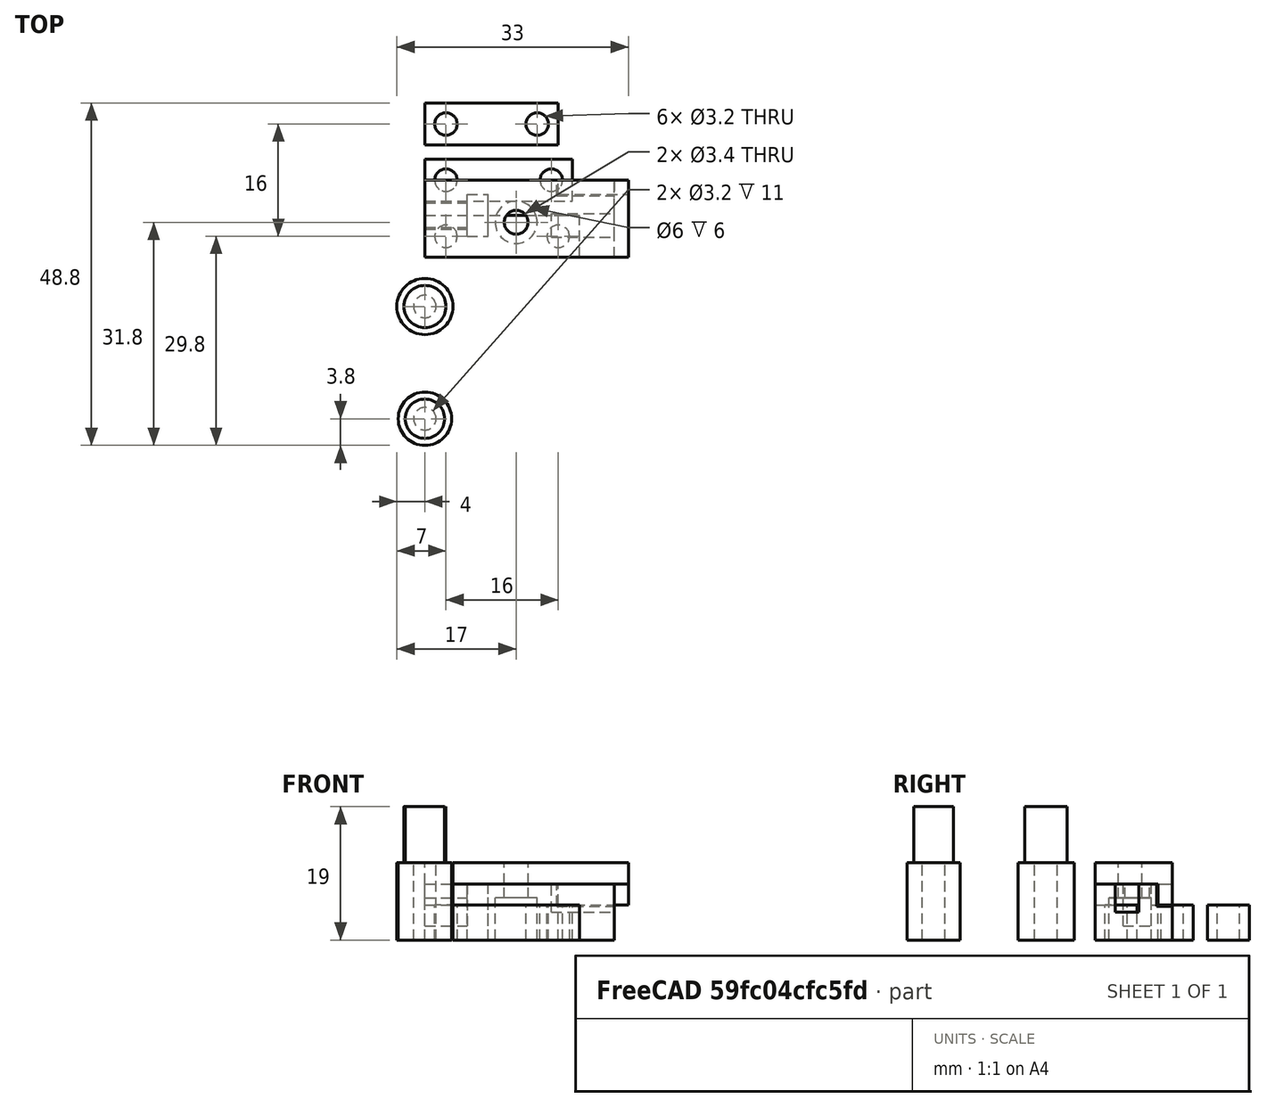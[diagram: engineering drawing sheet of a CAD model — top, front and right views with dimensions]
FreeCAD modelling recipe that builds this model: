
FCSTD DOCUMENT  (FreeCAD 0.19R24291 (Git))
Label: pb1
License: All rights reserved
LicenseURL: http://en.wikipedia.org/wiki/All_rights_reserved
objects: Part::Cylinder×15, Part::Box×11, Part::MultiFuse×7, Part::Cut×7
note: 40 computed .brp shape members not serialized (recipe doc carries the construction recipe); baked Part::Feature solids carry a one-line shape summary decoded from their .brp

FEATURE [Part::Box] Box  label="Cube"
  AttacherType = Attacher::AttachEngine3D
  Height = 8
  Length = 27
  Width = 11
FEATURE [Part::Box] Box001  label="Cube001"
  AttacherType = Attacher::AttachEngine3D
  Height = 6
  Length = 9
  Placement = pos=(0,4,2) rot=(0,0,1;0rad)
  Width = 4
FEATURE [Part::Box] Box002  label="Cube002"
  AttacherType = Attacher::AttachEngine3D
  Height = 4
  Length = 9
  Placement = pos=(18,2.85,4) rot=(0,0,1;0rad)
  Width = 3.4
FEATURE [Part::Box] Box003  label="Cube003"
  AttacherType = Attacher::AttachEngine3D
  Height = 8
  Length = 3
  Placement = pos=(6,3,0) rot=(0,0,1;0rad)
  Width = 6
FEATURE [Part::Cylinder] Cylinder
  Angle = 360
  AttacherType = Attacher::AttachEngine3D
  Height = 6
  Placement = pos=(13,5,0) rot=(0,0,1;0rad)
  Radius = 3
FEATURE [Part::Cylinder] Cylinder001
  Angle = 360
  AttacherType = Attacher::AttachEngine3D
  Height = 2
  Placement = pos=(13,5,6) rot=(0,0,1;0rad)
  Radius = 1.7
FEATURE [Part::Box] Box004  label="Cube004"
  AttacherType = Attacher::AttachEngine3D
  Height = 3
  Length = 29
  Placement = pos=(0,0,8) rot=(0,0,1;0rad)
  Width = 11
FEATURE [Part::Cylinder] Cylinder002
  Angle = 360
  AttacherType = Attacher::AttachEngine3D
  Height = 3
  Placement = pos=(13,5,8) rot=(0,0,1;0rad)
  Radius = 1.7
FEATURE [Part::Box] Box005  label="Cube005"
  AttacherType = Attacher::AttachEngine3D
  Height = 2
  Length = 6
  Placement = pos=(0,4.25,6) rot=(0,0,1;0rad)
  Width = 3.5
FEATURE [Part::Box] Box006  label="Cube006"
  AttacherType = Attacher::AttachEngine3D
  Height = 3
  Length = 10
  Placement = pos=(19,9,5) rot=(0,0,1;0rad)
  Width = 2
FEATURE [Part::MultiFuse] Fusion001
  Shapes = -> [Box004,Box005,Box006]
FEATURE [Part::Cut] Cut001
  Base = -> Fusion001
  Tool = -> Cylinder002
FEATURE [Part::Box] Box007  label="Cube007"
  AttacherType = Attacher::AttachEngine3D
  Height = 3.2
  Length = 10.2
  Placement = pos=(18.8,8.8,4.8) rot=(0,0,1;0rad)
  Width = 2.2
FEATURE [Part::MultiFuse] Fusion
  Shapes = -> [Box001,Box002,Box003,Cylinder,Cylinder001,Box007]
FEATURE [Part::Cut] Cut
  Base = -> Box
  Tool = -> Fusion
FEATURE [Part::Box] Box008  label="Cube008"
  AttacherType = Attacher::AttachEngine3D
  Height = 5
  Length = 22
  Width = 6
FEATURE [Part::Cylinder] Cylinder003
  Angle = 360
  AttacherType = Attacher::AttachEngine3D
  Height = 5
  Placement = pos=(3,3,0) rot=(0,0,1;0rad)
  Radius = 1.6
FEATURE [Part::Cylinder] Cylinder004
  Angle = 360
  AttacherType = Attacher::AttachEngine3D
  Height = 5
  Placement = pos=(19,3,0) rot=(0,0,1;0rad)
  Radius = 1.6
FEATURE [Part::MultiFuse] Fusion002
  Shapes = -> [Cylinder003,Cylinder004]
FEATURE [Part::Cut] Cut002
  Base = -> Box008
  Tool = -> Fusion002
FEATURE [Part::Box] Box009  label="Cube009"
  AttacherType = Attacher::AttachEngine3D
  Height = 5
  Length = 21
  Width = 6
FEATURE [Part::Cylinder] Cylinder005
  Angle = 360
  AttacherType = Attacher::AttachEngine3D
  Height = 5
  Placement = pos=(3,3,0) rot=(0,0,1;0rad)
  Radius = 1.6
FEATURE [Part::Cylinder] Cylinder006
  Angle = 360
  AttacherType = Attacher::AttachEngine3D
  Height = 5
  Placement = pos=(18,3,0) rot=(0,0,1;0rad)
  Radius = 1.6
FEATURE [Part::MultiFuse] Fusion003
  Shapes = -> [Cylinder005,Cylinder006]
FEATURE [Part::Cut] Cut003
  Base = -> Box009
  Placement = pos=(0,8,0) rot=(0,0,1;0rad)
  Tool = -> Fusion003
FEATURE [Part::Box] Box010  label="Cube010"
  AttacherType = Attacher::AttachEngine3D
  Height = 5
  Length = 19
  Width = 6
FEATURE [Part::Cylinder] Cylinder007
  Angle = 360
  AttacherType = Attacher::AttachEngine3D
  Height = 5
  Placement = pos=(3,3,0) rot=(0,0,1;0rad)
  Radius = 1.6
FEATURE [Part::Cylinder] Cylinder008
  Angle = 360
  AttacherType = Attacher::AttachEngine3D
  Height = 5
  Placement = pos=(16,3,0) rot=(0,0,1;0rad)
  Radius = 1.6
FEATURE [Part::MultiFuse] Fusion004
  Shapes = -> [Cylinder007,Cylinder008]
FEATURE [Part::Cut] Cut004
  Base = -> Box010
  Placement = pos=(0,16,0) rot=(0,0,1;0rad)
  Tool = -> Fusion004
FEATURE [Part::Cylinder] Cylinder009
  Angle = 360
  AttacherType = Attacher::AttachEngine3D
  Height = 11
  Placement = pos=(0,-7,0) rot=(0,0,1;0rad)
  Radius = 4
FEATURE [Part::Cylinder] Cylinder010
  Angle = 360
  AttacherType = Attacher::AttachEngine3D
  Height = 11
  Placement = pos=(0,-7,0) rot=(0,0,1;0rad)
  Radius = 1.6
FEATURE [Part::Cylinder] Cylinder011
  Angle = 360
  AttacherType = Attacher::AttachEngine3D
  Height = 8
  Placement = pos=(0,-7,11) rot=(0,0,1;0rad)
  Radius = 3
FEATURE [Part::MultiFuse] Fusion005
  Shapes = -> [Cylinder009,Cylinder011]
FEATURE [Part::Cut] Cut005
  Base = -> Fusion005
  Tool = -> Cylinder010
FEATURE [Part::Cylinder] Cylinder012
  Angle = 360
  AttacherType = Attacher::AttachEngine3D
  Height = 8
  Placement = pos=(0,-7,11) rot=(0,0,1;0rad)
  Radius = 2.8
FEATURE [Part::Cylinder] Cylinder013
  Angle = 360
  AttacherType = Attacher::AttachEngine3D
  Height = 11
  Placement = pos=(0,-7,0) rot=(0,0,1;0rad)
  Radius = 3.8
FEATURE [Part::MultiFuse] Fusion006
  Shapes = -> [Cylinder013,Cylinder012]
FEATURE [Part::Cylinder] Cylinder014
  Angle = 360
  AttacherType = Attacher::AttachEngine3D
  Height = 11
  Placement = pos=(0,-7,0) rot=(0,0,1;0rad)
  Radius = 1.6
FEATURE [Part::Cut] Cut006
  Base = -> Fusion006
  Placement = pos=(0,-16,0) rot=(0,0,1;0rad)
  Tool = -> Cylinder014
